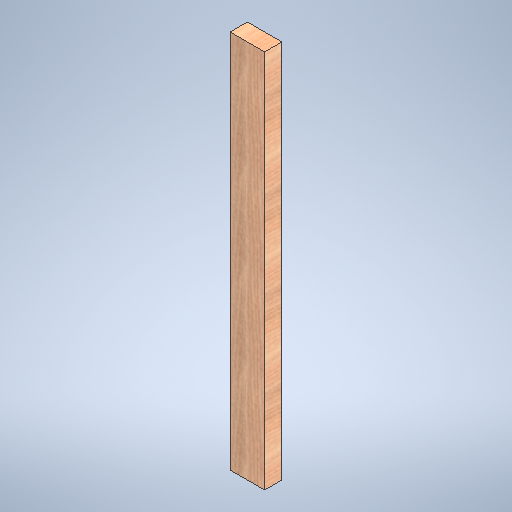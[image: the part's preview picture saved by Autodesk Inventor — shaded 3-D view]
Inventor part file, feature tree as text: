
AUTODESK INVENTOR PART (.ipt)
format: ipt  version: 2025 (Build 290162000, 162)  size: 316,928 bytes
history: native  units: in
note: dims shown in document units (in); Inventor stores cm internally (conversion verified against a paired STEP export)
features: extrude x1, sketch x1
ambient origin geometry x8: Origin, YZ Plane, XZ Plane, XY Plane, X Axis, Y Axis, Z Axis, Center Point
bodies: Solid1 (feature_tree)
feature tree (2):
  extrude  "Extrusion1"  Depth=44.0in
  sketch  "Sketch1"  dims[d0=4.0in d1=44.0in d2=2.0in d3=0.0in]
